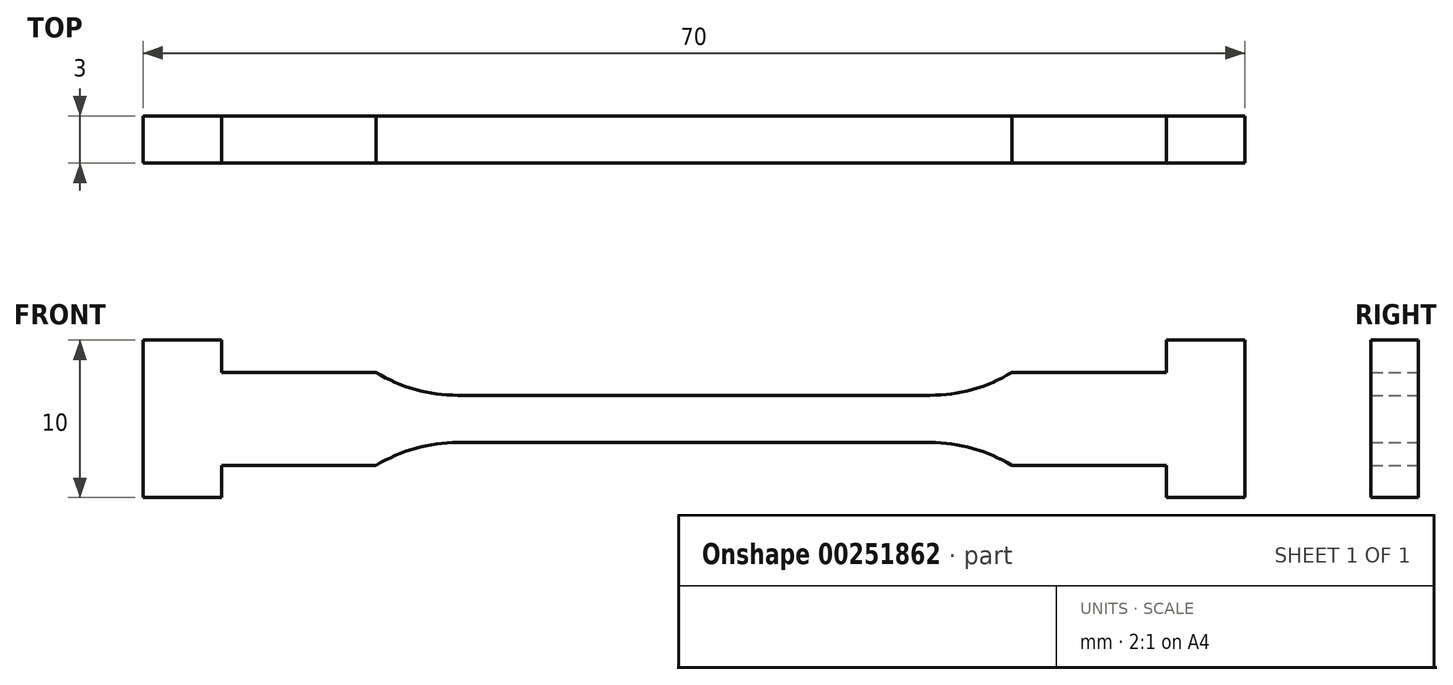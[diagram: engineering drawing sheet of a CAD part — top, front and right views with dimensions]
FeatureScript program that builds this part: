
annotation { "Feature Type Name" : "Feature", "Feature Type Description" : "" }
export const myFeature = defineFeature(function(context is Context, id is Id, definition is map)
    precondition{}
    {
        {
            var Q0;
            Q0=qCreatedBy(makeId("Front.planeOp"),FACE);
            var sketch = newSketch(context, id + "F0", { "sketchPlane" : qUnion([Q0])});
            skLineSegment(sketch, "E0.left", {"start": v(35, 1.5) * mm, "end": v(35, -1.5) * mm});
            skLineSegment(sketch, "E0.right", {"start": v(-35, 1.5) * mm, "end": v(-35, -1.5) * mm});
            skPoint(sketch, "E0.middle", {"position": v(0, 0) * mm});
            skPoint(sketch, "E1.endSnap0", {"position": v(-35, 0) * mm});
            skLineSegment(sketch, "E2.bottom", {"start": v(-35, 5) * mm, "end": v(-30, 5) * mm});
            skLineSegment(sketch, "E2.top", {"start": v(-35, -5) * mm, "end": v(-30, -5) * mm});
            skLineSegment(sketch, "E2.left", {"start": v(-35, 5) * mm, "end": v(-35, -5) * mm});
            skLineSegment(sketch, "E2.right", {"start": v(-30, 5) * mm, "end": v(-30, 2.95) * mm});
            skPoint(sketch, "E2.middle", {"position": v(-32.5, 0) * mm});
            skLineSegment(sketch, "E3.left", {"start": v(-32, 0) * mm, "end": v(-32, 0) * mm});
            skLineSegment(sketch, "E3.right", {"start": v(-33, 0) * mm, "end": v(-33, 0) * mm});
            skPoint(sketch, "E4.endSnap0", {"position": v(35, 0) * mm});
            skLineSegment(sketch, "E5.bottom", {"start": v(35, 5) * mm, "end": v(30, 5) * mm});
            skLineSegment(sketch, "E5.top", {"start": v(35, -5) * mm, "end": v(30, -5) * mm});
            skLineSegment(sketch, "E5.left", {"start": v(35, 5) * mm, "end": v(35, -5) * mm});
            skLineSegment(sketch, "E5.right", {"start": v(30, 5) * mm, "end": v(30, 2.95) * mm});
            skPoint(sketch, "E5.middle", {"position": v(32.5, 0) * mm});
            skLineSegment(sketch, "E6.bottom", {"start": v(-30, 2.95) * mm, "end": v(-20.19, 2.95) * mm});
            skLineSegment(sketch, "E6.top", {"start": v(-30, -2.95) * mm, "end": v(-20.19, -2.95) * mm});
            skPoint(sketch, "E6.middle", {"position": v(-22.5, 0) * mm});
            skLineSegment(sketch, "E7.bottom", {"start": v(30, 2.95) * mm, "end": v(20.19, 2.95) * mm});
            skLineSegment(sketch, "E7.top", {"start": v(30, -2.95) * mm, "end": v(20.19, -2.95) * mm});
            skPoint(sketch, "E7.middle", {"position": v(22.5, 0) * mm});
            skArc(sketch, "E8", {"start": v(-20.19, 2.95) * mm, "mid": v(-17.7, 1.87) * mm, "end": v(-15, 1.5) * mm});
            skArc(sketch, "E9", {"start": v(-15, -1.5) * mm, "mid": v(-17.7, -1.87) * mm, "end": v(-20.19, -2.95) * mm});
            skPoint(sketch, "E10.end.orphan", {"position": v(-15, 2.95) * mm});
            skPoint(sketch, "E11.orphan", {"position": v(-15, -2.95) * mm});
            skPoint(sketch, "E12.start.orphan", {"position": v(-30, 0) * mm});
            skLineSegment(sketch, "E13.trimOffspring", {"start": v(-30, -2.95) * mm, "end": v(-30, -5) * mm});
            skArc(sketch, "E14", {"start": v(15, 1.5) * mm, "mid": v(17.7, 1.87) * mm, "end": v(20.19, 2.95) * mm});
            skArc(sketch, "E15", {"start": v(20.19, -2.95) * mm, "mid": v(17.7, -1.87) * mm, "end": v(15, -1.5) * mm});
            skPoint(sketch, "E7.right.start.orphan", {"position": v(15, 2.95) * mm});
            skLineSegment(sketch, "E16.trimOffspring", {"start": v(15, 1.5) * mm, "end": v(-15, 1.5) * mm});
            skLineSegment(sketch, "E17.trimOffspring", {"start": v(15, -1.5) * mm, "end": v(-15, -1.5) * mm});
            skPoint(sketch, "E18.trimOffspring.end.orphan", {"position": v(15, -2.95) * mm});
            skLineSegment(sketch, "E19.trimOffspring", {"start": v(30, -2.95) * mm, "end": v(30, -5) * mm});
            skPoint(sketch, "E20.start.orphan", {"position": v(30, 0) * mm});
            skPoint(sketch, "E4.start.orphan", {"position": v(35, 0) * mm});
            skSolve(sketch);
        }
        {
            var Q0;
            {var subQ0=sQuery(id+"F0.wireOp",EDGE,"E2.bottom");Q0=makeQuery(id+"F0.imprint","IMPRINT",FACE,{"disambiguationData":[TD([[makeQuery(id+"F0.imprint","IMPRINT",EDGE,{"derivedFrom":subQ0}),-1.0]])]});}
            extrude(context, id + "F1", {"entities" : qUnion([Q0]), "depth" : 3 * mm});
        }
    });
